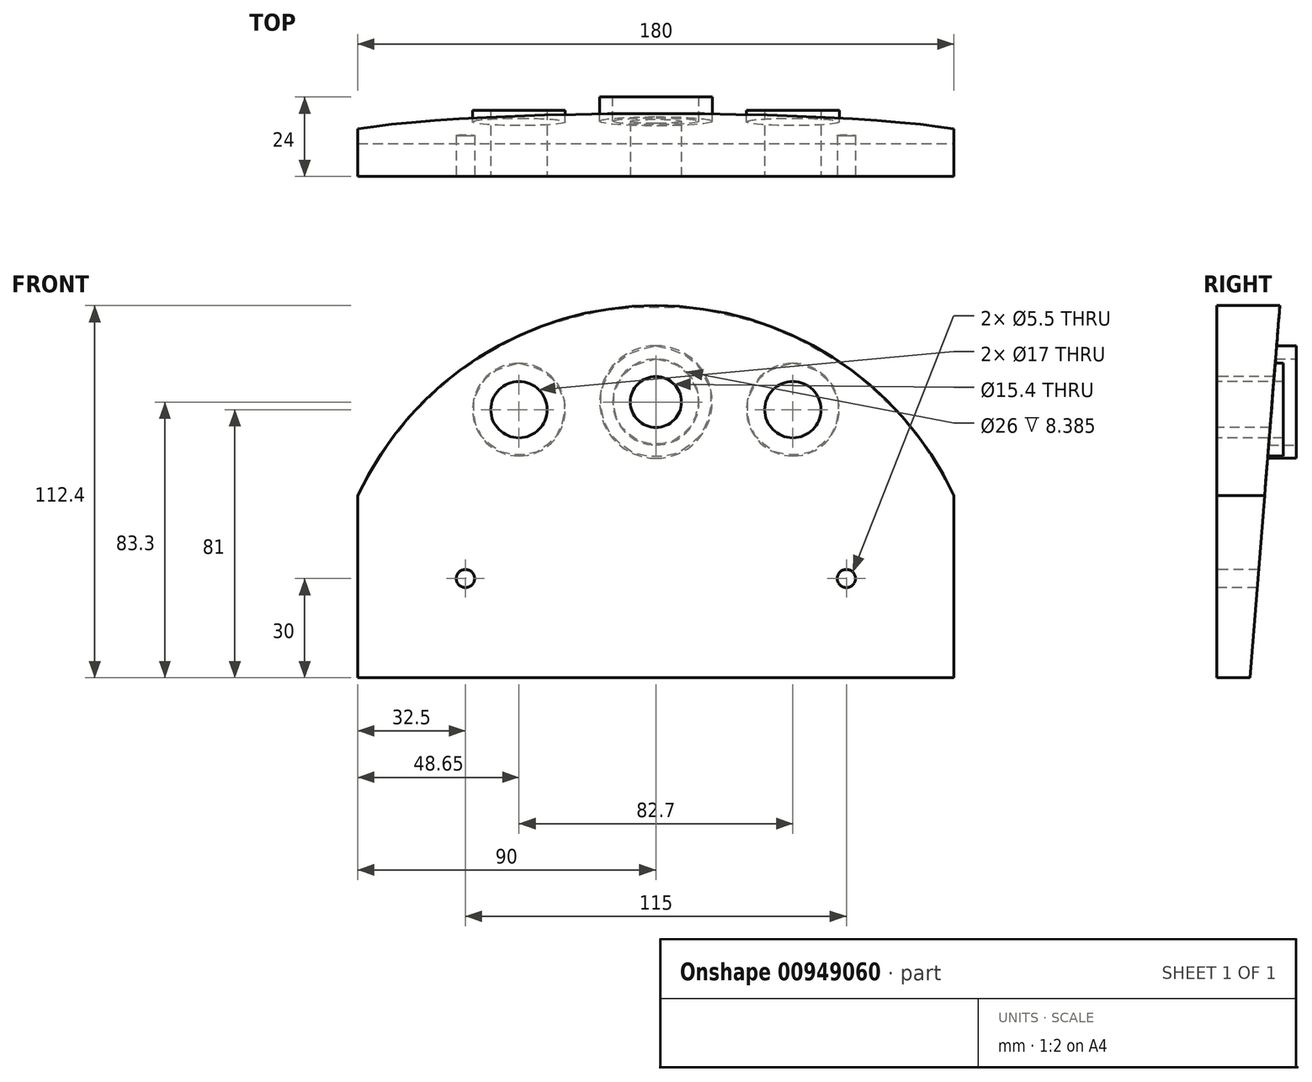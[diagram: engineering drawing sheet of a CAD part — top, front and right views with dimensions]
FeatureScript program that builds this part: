
annotation { "Feature Type Name" : "Feature", "Feature Type Description" : "" }
export const myFeature = defineFeature(function(context is Context, id is Id, definition is map)
    precondition{}
    {
        {
            var Q0;
            Q0=qCreatedBy(makeId("Front.planeOp"),FACE);
            var sketch = newSketch(context, id + "F0", { "sketchPlane" : qUnion([Q0])});
            skLineSegment(sketch, "E0.bottom", {"start": v(0, 0) * mm, "end": v(180, 0) * mm});
            skLineSegment(sketch, "E0.top", {"start": v(0, 55) * mm, "end": v(180, 55) * mm, "construction": true});
            skLineSegment(sketch, "E0.left", {"start": v(0, 0) * mm, "end": v(0, 55) * mm});
            skLineSegment(sketch, "E0.right", {"start": v(180, 0) * mm, "end": v(180, 55) * mm});
            skArc(sketch, "E1", {"start": v(180, 55) * mm, "mid": v(90, 112.4) * mm, "end": v(0, 55) * mm});
            skSolve(sketch);
        }
        {
            var Q0;
            Q0 = qSketchRegion(id + "F0", true);
            extrude(context, id + "F1", {"entities" : qUnion([Q0]), "depth" : 19 * mm, "offsetDistance" : 25 * mm});
        }
        {
            var Q0;
            Q0=makeQuery(id+"F1.opExtrude","SWEPT_FACE",FACE,{"disambiguationData":[OSD([sQuery(id+"F0.wireOp",EDGE,"E0.right")])]});
            var sketch = newSketch(context, id + "F2", { "sketchPlane" : qUnion([Q0])});
            skLineSegment(sketch, "E2", {"start": v(-9, 0) * mm, "end": v(0, 112.4) * mm});
            skLineSegment(sketch, "E3", {"start": v(0, 112.4) * mm, "end": v(0, 0) * mm});
            skLineSegment(sketch, "E4", {"start": v(0, 0) * mm, "end": v(-9, 0) * mm});
            skSolve(sketch);
        }
        {
            var Q0;
            Q0 = qSketchRegion(id + "F2", true);
            extrude(context, id + "F3", {"entities" : qUnion([Q0]), "operationType" : NewBodyOperationType.REMOVE, "endBound" : BoundingType.THROUGH_ALL, "oppositeDirection" : true, "depth" : 25 * mm, "offsetDistance" : 25 * mm});
        }
        {
            var Q0;
            Q0=makeQuery(id+"F1.opExtrude","CAP_FACE",FACE,{"disambiguationData":[OSD([sQuery(id+"F0.wireOp",EDGE,"E0.bottom"),sQuery(id+"F0.wireOp",EDGE,"E0.left"),sQuery(id+"F0.wireOp",EDGE,"E0.right"),sQuery(id+"F0.wireOp",EDGE,"E1")])],"isStart":false});
            var sketch = newSketch(context, id + "F4", { "sketchPlane" : qUnion([Q0])});
            skPoint(sketch, "E5", {"position": v(32.5, 30) * mm});
            skPoint(sketch, "E6", {"position": v(147.5, 30) * mm});
            skLineSegment(sketch, "E7", {"start": v(32.5, 30) * mm, "end": v(147.5, 30) * mm});
            skSolve(sketch);
        }
        {
            var Q0;
            Q0=sQuery(id+"F4.wireOp",VERTEX,"E5");
            var Q1;
            Q1=sQuery(id+"F4.wireOp",VERTEX,"E6");
            var Q2;
            Q2=makeQuery(id+"F1.opExtrude","SWEPT_BODY",BODY,{"disambiguationData":[OSD([sQuery(id+"F0.wireOp",EDGE,"E0.bottom"),sQuery(id+"F0.wireOp",EDGE,"E0.left"),sQuery(id+"F0.wireOp",EDGE,"E0.right"),sQuery(id+"F0.wireOp",EDGE,"E1")])]});
            hole(context, id + "F5", {"style" : HoleStyle.SIMPLE, "endStyle" : HoleEndStyle.THROUGH, "standardTappedOrClearance" : lookupTablePath({ "fit" : "Normal", "standard" : "ISO", "size" : "M5", "type" : "Clearance" }), "standardBlindInLast" : lookupTablePath({ "fit" : "Normal", "standard" : "ISO", "engagement" : "75%", "pitch" : "0.8 mm", "size" : "M5", "type" : "Clearance & tapped" }), "holeDiameter" : 5.5 * mm, "majorDiameter" : 5 * mm, "isTappedThrough" : true, "tappedDepth" : 12 * mm, "tapClearance" : 3, "locations" : qUnion([Q0, Q1]), "scope" : qUnion([Q2])});
        }
        {
            var Q0;
            Q0=makeQuery(id+"F1.opExtrude","CAP_FACE",FACE,{"disambiguationData":[OSD([sQuery(id+"F0.wireOp",EDGE,"E0.bottom"),sQuery(id+"F0.wireOp",EDGE,"E0.left"),sQuery(id+"F0.wireOp",EDGE,"E0.right"),sQuery(id+"F0.wireOp",EDGE,"E1")])],"isStart":false});
            var sketch = newSketch(context, id + "F6", { "sketchPlane" : qUnion([Q0])});
            skCircle(sketch, "E8", {"center": v(90, 83.3) * mm, "radius": 7.7 * mm});
            skPoint(sketch, "E8.centerSnap0", {"position": v(90, 112.4) * mm});
            skCircle(sketch, "E9", {"center": v(131.35, 81) * mm, "radius": 8.5 * mm});
            skCircle(sketch, "E10", {"center": v(48.65, 81) * mm, "radius": 8.5 * mm});
            skLineSegment(sketch, "E11", {"start": v(48.65, 81) * mm, "end": v(131.35, 81) * mm, "construction": true});
            skLineSegment(sketch, "E12", {"start": v(90, 83.3) * mm, "end": v(90, 81) * mm, "construction": true});
            skLineSegment(sketch, "E13", {"start": v(90, 81) * mm, "end": v(90, 0) * mm, "construction": true});
            skSolve(sketch);
        }
        {
            var Q0;
            Q0 = qSketchRegion(id + "F6", true);
            extrude(context, id + "F7", {"entities" : qUnion([Q0]), "operationType" : NewBodyOperationType.REMOVE, "endBound" : BoundingType.THROUGH_ALL, "oppositeDirection" : true, "depth" : 25 * mm, "offsetDistance" : 25 * mm});
        }
        {
            var Q0;
            Q0=makeQuery(id+"F1.opExtrude","CAP_FACE",FACE,{"disambiguationData":[OSD([sQuery(id+"F0.wireOp",EDGE,"E0.bottom"),sQuery(id+"F0.wireOp",EDGE,"E0.left"),sQuery(id+"F0.wireOp",EDGE,"E0.right"),sQuery(id+"F0.wireOp",EDGE,"E1")])],"isStart":false});
            cPlane(context, id + "F8", {"entities" : qUnion([Q0]), "cplaneType" : CPlaneType.OFFSET, "offset" : 24 * mm, "oppositeDirection" : true, "width" : 150 * mm, "height" : 150 * mm});
        }
        {
            var Q0;
            Q0=qCreatedBy(id+"F8.planeOp",FACE);
            var sketch = newSketch(context, id + "F9", { "sketchPlane" : qUnion([Q0])});
            skCircle(sketch, "E14", {"center": v(90, 83.3) * mm, "radius": 17 * mm});
            skCircle(sketch, "E15", {"center": v(90, 83.3) * mm, "radius": 13 * mm});
            skSolve(sketch);
        }
        {
            var Q0;
            Q0 = qSketchRegion(id + "F9", true);
            extrude(context, id + "F10", {"entities" : qUnion([Q0]), "operationType" : NewBodyOperationType.ADD, "endBound" : BoundingType.UP_TO_NEXT, "depth" : 25 * mm, "offsetDistance" : 25 * mm});
        }
        {
            var Q0;
            Q0=makeQuery(id+"F1.opExtrude","CAP_FACE",FACE,{"disambiguationData":[OSD([sQuery(id+"F0.wireOp",EDGE,"E0.bottom"),sQuery(id+"F0.wireOp",EDGE,"E0.left"),sQuery(id+"F0.wireOp",EDGE,"E0.right"),sQuery(id+"F0.wireOp",EDGE,"E1")])],"isStart":false});
            cPlane(context, id + "F11", {"entities" : qUnion([Q0]), "cplaneType" : CPlaneType.OFFSET, "offset" : 20 * mm, "oppositeDirection" : true, "width" : 150 * mm, "height" : 150 * mm});
        }
        {
            var Q0;
            Q0=qCreatedBy(id+"F11.planeOp",FACE);
            var sketch = newSketch(context, id + "F12", { "sketchPlane" : qUnion([Q0])});
            skCircle(sketch, "E16", {"center": v(131.35, 81) * mm, "radius": 14 * mm});
            skCircle(sketch, "E17", {"center": v(48.65, 81) * mm, "radius": 14 * mm});
            skCircle(sketch, "E18", {"center": v(48.65, 81) * mm, "radius": 8.5 * mm});
            skCircle(sketch, "E19", {"center": v(131.35, 81) * mm, "radius": 8.5 * mm});
            skSolve(sketch);
        }
        {
            var Q0;
            Q0 = qSketchRegion(id + "F12", true);
            extrude(context, id + "F13", {"entities" : qUnion([Q0]), "operationType" : NewBodyOperationType.ADD, "endBound" : BoundingType.UP_TO_NEXT, "depth" : 25 * mm, "offsetDistance" : 25 * mm});
        }
    });
